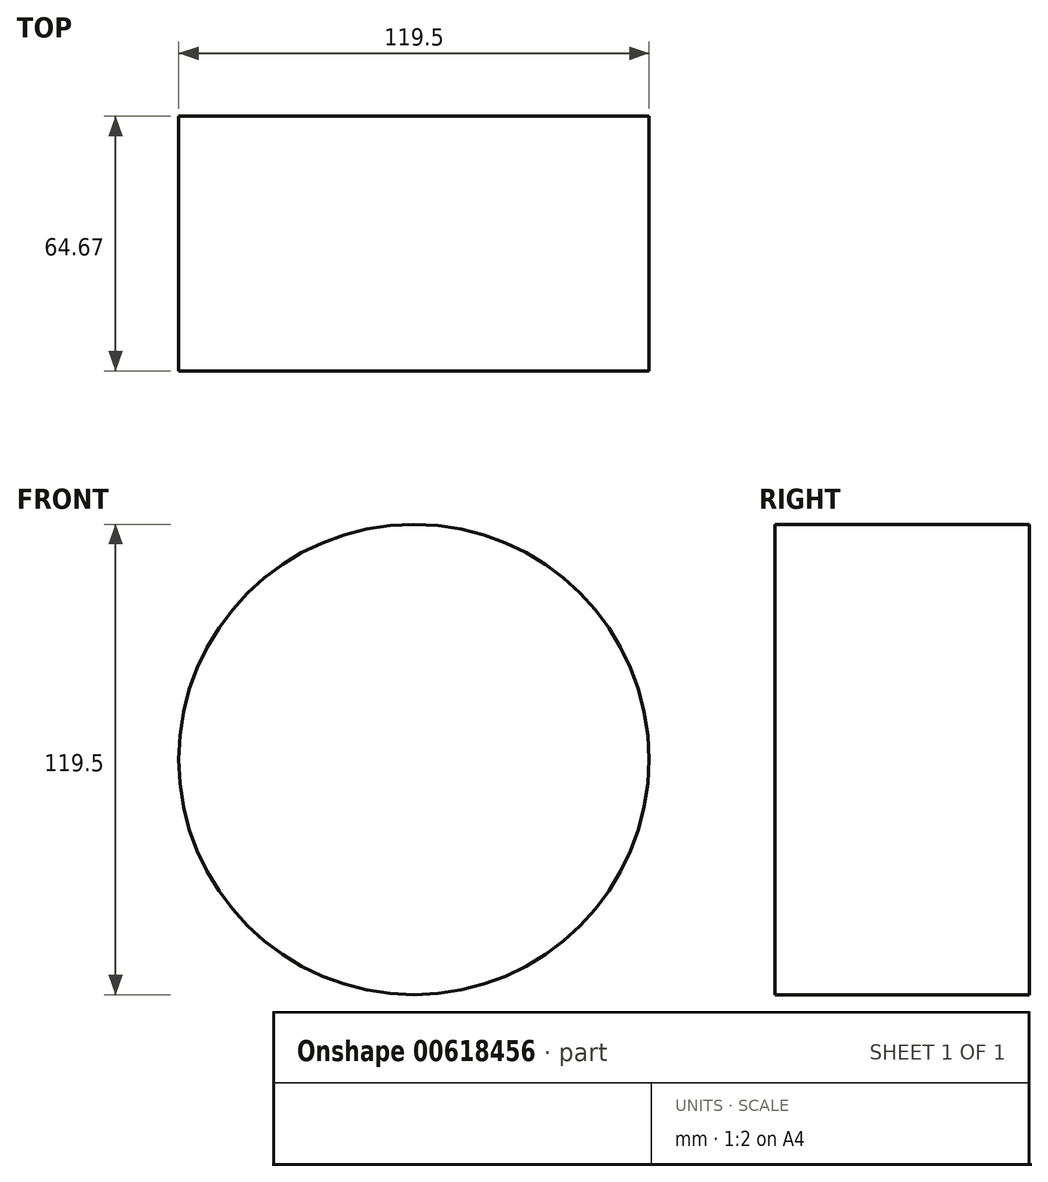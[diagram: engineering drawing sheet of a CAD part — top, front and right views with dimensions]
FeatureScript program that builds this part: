
annotation { "Feature Type Name" : "Feature", "Feature Type Description" : "" }
export const myFeature = defineFeature(function(context is Context, id is Id, definition is map)
    precondition{}
    {
        {
            var Q0;
            Q0=qCreatedBy(makeId("Front.planeOp"),FACE);
            var sketch = newSketch(context, id + "F0", { "sketchPlane" : qUnion([Q0])});
            skCircle(sketch, "E0", {"center": v(0, 0) * mm, "radius": 59.75 * mm});
            skCircle(sketch, "E1", {"center": v(0, 0) * mm, "radius": 54.54 * mm});
            skSolve(sketch);
        }
        {
            var Q0;
            Q0=sQuery(id+"F0.wireOp",EDGE,"E0");
            extrude(context, id + "F1", {"bodyType" : ToolBodyType.SURFACE, "surfaceEntities" : qUnion([Q0]), "depth" : 64.67 * mm, "offsetDistance" : 25.4 * mm});
        }
    });
